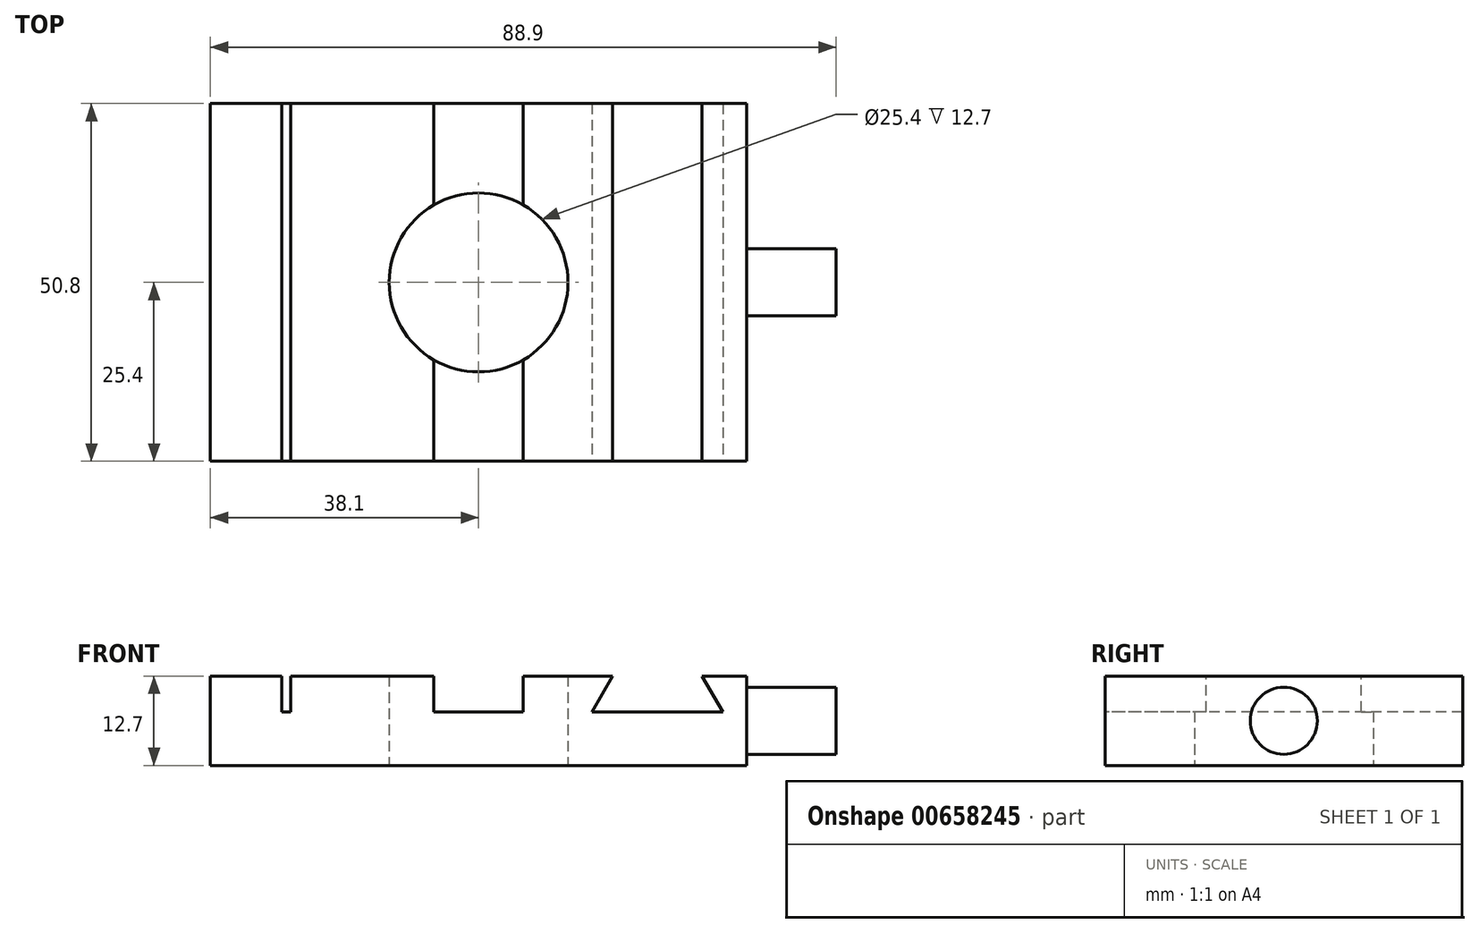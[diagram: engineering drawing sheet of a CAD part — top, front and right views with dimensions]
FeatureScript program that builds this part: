
annotation { "Feature Type Name" : "Feature", "Feature Type Description" : "" }
export const myFeature = defineFeature(function(context is Context, id is Id, definition is map)
    precondition{}
    {
        {
            var Q0;
            Q0=qCreatedBy(makeId("Top.planeOp"),FACE);
            var sketch = newSketch(context, id + "F0", { "sketchPlane" : qUnion([Q0])});
            skLineSegment(sketch, "E0.bottom", {"start": v(38.1, -25.4) * mm, "end": v(-38.1, -25.4) * mm});
            skLineSegment(sketch, "E0.top", {"start": v(38.1, 25.4) * mm, "end": v(-38.1, 25.4) * mm});
            skLineSegment(sketch, "E0.left", {"start": v(38.1, -25.4) * mm, "end": v(38.1, 25.4) * mm});
            skLineSegment(sketch, "E0.right", {"start": v(-38.1, -25.4) * mm, "end": v(-38.1, 25.4) * mm});
            skPoint(sketch, "E0.middle", {"position": v(0, 0) * mm});
            skCircle(sketch, "E1", {"center": v(0, 0) * mm, "radius": 12.7 * mm});
            skSolve(sketch);
        }
        {
            var Q0;
            Q0=makeQuery(id+"F0.imprint","IMPRINT",FACE,{"disambiguationData":[TD([[makeQuery(id+"F0.imprint","IMPRINT",EDGE,{"derivedFrom":sQuery(id+"F0.wireOp",EDGE,"E0.bottom")}),-1.0]])]});
            extrude(context, id + "F1", {"entities" : qUnion([Q0]), "depth" : 12.7 * mm, "offsetDistance" : 25.4 * mm});
        }
        {
            var Q0;
            Q0=makeQuery(id+"F1.opExtrude","CAP_FACE",FACE,{"disambiguationData":[OSD([sQuery(id+"F0.wireOp",EDGE,"E0.bottom"),sQuery(id+"F0.wireOp",EDGE,"E0.top"),sQuery(id+"F0.wireOp",EDGE,"E0.left"),sQuery(id+"F0.wireOp",EDGE,"E0.right"),sQuery(id+"F0.wireOp",EDGE,"E1")])],"isStart":false});
            var sketch = newSketch(context, id + "F2", { "sketchPlane" : qUnion([Q0])});
            skLineSegment(sketch, "E2.bottom", {"start": v(-27.94, 25.4) * mm, "end": v(-26.67, 25.4) * mm});
            skLineSegment(sketch, "E2.top", {"start": v(-27.94, -25.4) * mm, "end": v(-26.67, -25.4) * mm});
            skLineSegment(sketch, "E2.left", {"start": v(-27.94, 25.4) * mm, "end": v(-27.94, -25.4) * mm});
            skLineSegment(sketch, "E2.right", {"start": v(-26.67, 25.4) * mm, "end": v(-26.67, -25.4) * mm});
            skLineSegment(sketch, "E3", {"start": v(-6.35, 25.4) * mm, "end": v(-6.35, -25.4) * mm});
            skLineSegment(sketch, "E4", {"start": v(-6.35, -25.4) * mm, "end": v(6.35, -25.4) * mm});
            skLineSegment(sketch, "E5", {"start": v(6.35, 25.4) * mm, "end": v(-6.35, 25.4) * mm});
            skLineSegment(sketch, "E6", {"start": v(6.35, 25.4) * mm, "end": v(6.35, -25.4) * mm});
            skPoint(sketch, "E7", {"position": v(0, 0) * mm});
            skLineSegment(sketch, "E8", {"start": v(0, 25.4) * mm, "end": v(0, -25.4) * mm, "construction": true});
            skSolve(sketch);
        }
        {
            var Q0;
            Q0=makeQuery(id+"F2.imprint","IMPRINT",FACE,{"disambiguationData":[TD([[makeQuery(id+"F2.imprint","IMPRINT",EDGE,{"derivedFrom":sQuery(id+"F2.wireOp",EDGE,"E2.bottom")}),1.0]])]});
            var Q1;
            {var subQ0=sQuery(id+"F2.wireOp",EDGE,"E4");Q1=makeQuery(id+"F2.imprint","IMPRINT",FACE,{"disambiguationData":[TD([[makeQuery(id+"F2.imprint","IMPRINT",EDGE,{"derivedFrom":subQ0}),-1.0]])]});}
            var Q2;
            {var subQ0=sQuery(id+"F2.wireOp",EDGE,"E5");Q2=makeQuery(id+"F2.imprint","IMPRINT",FACE,{"disambiguationData":[TD([[makeQuery(id+"F2.imprint","IMPRINT",EDGE,{"derivedFrom":subQ0}),1.0]])]});}
            extrude(context, id + "F3", {"entities" : qUnion([Q0, Q1, Q2]), "operationType" : NewBodyOperationType.REMOVE, "oppositeDirection" : true, "depth" : 5.08 * mm, "offsetDistance" : 25.4 * mm});
        }
        {
            var Q0;
            Q0=makeQuery(id+"F1.opExtrude","SWEPT_FACE",FACE,{"disambiguationData":[OSD([sQuery(id+"F0.wireOp",EDGE,"E0.bottom")])]});
            var sketch = newSketch(context, id + "F4", { "sketchPlane" : qUnion([Q0])});
            skLineSegment(sketch, "E9", {"start": v(19.05, 12.7) * mm, "end": v(16.12, 7.62) * mm});
            skLineSegment(sketch, "E10", {"start": v(16.12, 7.62) * mm, "end": v(34.68, 7.62) * mm});
            skLineSegment(sketch, "E11", {"start": v(34.68, 7.62) * mm, "end": v(31.75, 12.7) * mm});
            skLineSegment(sketch, "E12", {"start": v(31.75, 12.7) * mm, "end": v(19.05, 12.7) * mm});
            skLineSegment(sketch, "E13", {"start": v(25.4, 7.62) * mm, "end": v(25.4, 12.7) * mm, "construction": true});
            skSolve(sketch);
        }
        {
            var Q0;
            Q0=makeQuery(id+"F4.imprint","IMPRINT",FACE,{"disambiguationData":[TD([[makeQuery(id+"F4.imprint","IMPRINT",EDGE,{"derivedFrom":sQuery(id+"F4.wireOp",EDGE,"E9")}),1.0]])]});
            extrude(context, id + "F5", {"entities" : qUnion([Q0]), "operationType" : NewBodyOperationType.REMOVE, "endBound" : BoundingType.THROUGH_ALL, "oppositeDirection" : true, "depth" : 25.4 * mm, "offsetDistance" : 25.4 * mm});
        }
        {
            var Q0;
            Q0=makeQuery(id+"F1.opExtrude","SWEPT_FACE",FACE,{"disambiguationData":[OSD([sQuery(id+"F0.wireOp",EDGE,"E0.left")])]});
            var sketch = newSketch(context, id + "F6", { "sketchPlane" : qUnion([Q0])});
            skCircle(sketch, "E14", {"center": v(0, 6.35) * mm, "radius": 4.76 * mm});
            skPoint(sketch, "E14.centerSnap0", {"position": v(-25.4, 6.35) * mm});
            skPoint(sketch, "E14.centerSnap1", {"position": v(0, 12.7) * mm});
            skSolve(sketch);
        }
        {
            var Q0;
            Q0=makeQuery(id+"F6.imprint","IMPRINT",FACE,{"disambiguationData":[TD([[makeQuery(id+"F6.imprint","IMPRINT",EDGE,{"derivedFrom":sQuery(id+"F6.wireOp",EDGE,"E14")}),1.0]])]});
            extrude(context, id + "F7", {"entities" : qUnion([Q0]), "operationType" : NewBodyOperationType.ADD, "depth" : 12.7 * mm, "offsetDistance" : 25.4 * mm});
        }
    });
